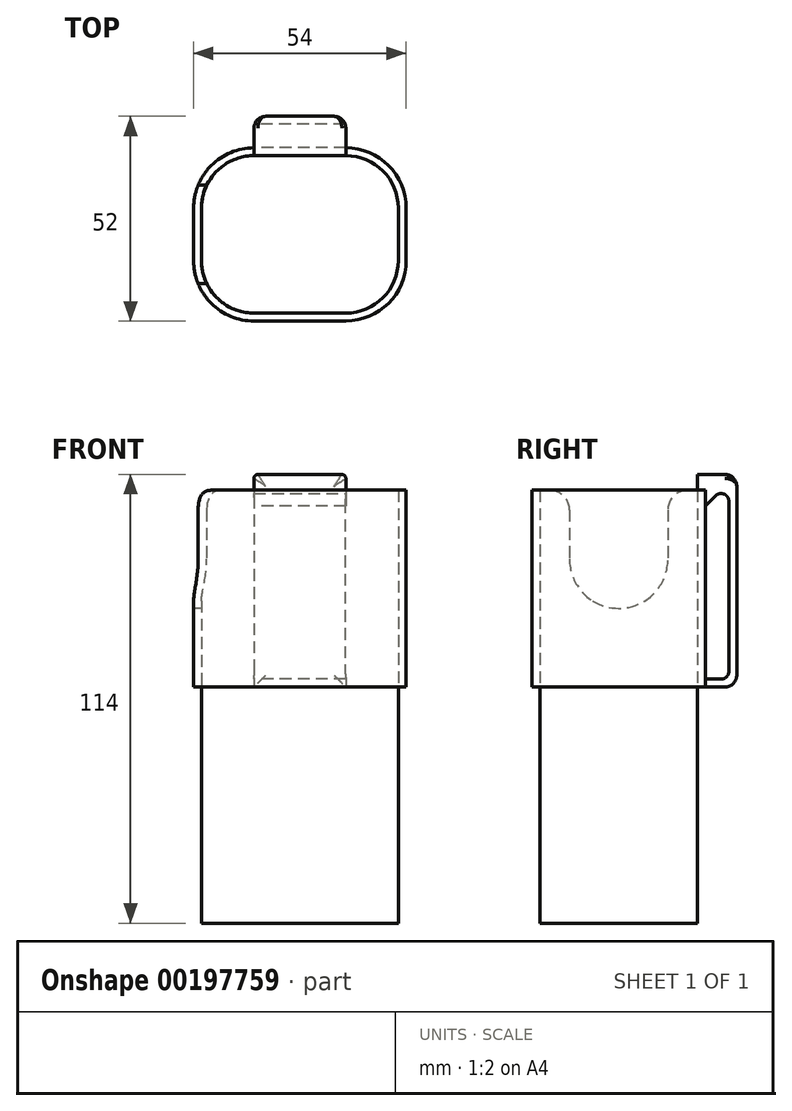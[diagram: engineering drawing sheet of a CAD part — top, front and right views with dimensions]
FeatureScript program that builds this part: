
annotation { "Feature Type Name" : "Feature", "Feature Type Description" : "" }
export const myFeature = defineFeature(function(context is Context, id is Id, definition is map)
    precondition{}
    {
        {
            assignVariable(context, id + "F0", {"name" : "WIDTH", "anyValue" : 50});
        }
        {
            assignVariable(context, id + "F1", {"name" : "DEPTH", "anyValue" : 40});
        }
        {
            var Q0;
            Q0=qCreatedBy(makeId("Top.planeOp"),FACE);
            var sketch = newSketch(context, id + "F2", { "sketchPlane" : qUnion([Q0])});
            skLineSegment(sketch, "E0.bottom", {"start": v(11.67, -40) * mm, "end": v(-11.67, -40) * mm});
            skLineSegment(sketch, "E0.top", {"start": v(11.67, 0) * mm, "end": v(-11.67, 0) * mm});
            skLineSegment(sketch, "E0.left", {"start": v(25, -26.67) * mm, "end": v(25, -13.33) * mm});
            skLineSegment(sketch, "E0.right", {"start": v(-25, -26.67) * mm, "end": v(-25, -13.33) * mm});
            skPoint(sketch, "E0.middle", {"position": v(0, -20) * mm});
            skPoint(sketch, "E1.visualSharp", {"position": v(-25, -40) * mm});
            skArc(sketch, "E1.filletArc", {"start": v(-25, -26.67) * mm, "mid": v(-21.1, -36.1) * mm, "end": v(-11.67, -40) * mm});
            skPoint(sketch, "E2.visualSharp", {"position": v(25, -40) * mm});
            skArc(sketch, "E2.filletArc", {"start": v(11.67, -40) * mm, "mid": v(21.1, -36.1) * mm, "end": v(25, -26.67) * mm});
            skPoint(sketch, "E3.visualSharp", {"position": v(-25, 0) * mm});
            skArc(sketch, "E3.filletArc", {"start": v(-11.67, 0) * mm, "mid": v(-21.1, -3.9) * mm, "end": v(-25, -13.33) * mm});
            skPoint(sketch, "E4.visualSharp", {"position": v(25, 0) * mm});
            skArc(sketch, "E4.filletArc", {"start": v(25, -13.33) * mm, "mid": v(21.1, -3.9) * mm, "end": v(11.67, 0) * mm});
            skSolve(sketch);
        }
        {
            var Q0;
            Q0=qSketchRegion(id+"F2",true);
            extrude(context, id + "F3", {"entities" : qUnion([Q0]), "endBound" : BoundingType.SYMMETRIC, "depth" : 120 * mm, "hasSecondDirection" : true, "secondDirectionOppositeDirection" : true, "secondDirectionDepth" : 25 * mm});
        }
        {
            assignVariable(context, id + "F4", {"name" : "THICKNESS", "anyValue" : 2});
        }
        {
            assignVariable(context, id + "F5", {"name" : "BELT_HOLE_THICKNESS", "anyValue" : 6});
        }
        {
            var Q0;
            Q0=qCreatedBy(makeId("Top.planeOp"),FACE);
            cPlane(context, id + "F6", {"entities" : qUnion([Q0]), "cplaneType" : CPlaneType.OFFSET, "offset" : 50 * mm, "width" : 150 * mm, "height" : 150 * mm});
        }
        {
            var Q0;
            Q0=qCreatedBy(makeId("Top.planeOp"),FACE);
            var sketch = newSketch(context, id + "F7", { "sketchPlane" : qUnion([Q0])});
            skLineSegment(sketch, "E5.0", {"start": v(27, -26.67) * mm, "end": v(27, -13.33) * mm});
            skArc(sketch, "E5.1", {"start": v(11.67, -42) * mm, "mid": v(22.5, -37.5) * mm, "end": v(27, -26.67) * mm});
            skArc(sketch, "E5.2", {"start": v(27, -13.33) * mm, "mid": v(22.5, -2.5) * mm, "end": v(11.67, 2) * mm});
            skLineSegment(sketch, "E5.3", {"start": v(-11.67, -42) * mm, "end": v(11.67, -42) * mm});
            skLineSegment(sketch, "E5.4", {"start": v(11.67, 2) * mm, "end": v(-11.67, 2) * mm});
            skArc(sketch, "E5.5", {"start": v(-11.67, 2) * mm, "mid": v(-22.5, -2.5) * mm, "end": v(-27, -13.33) * mm});
            skLineSegment(sketch, "E5.6", {"start": v(-27, -13.33) * mm, "end": v(-27, -26.67) * mm});
            skArc(sketch, "E5.7", {"start": v(-27, -26.67) * mm, "mid": v(-22.5, -37.5) * mm, "end": v(-11.67, -42) * mm});
            skSolve(sketch);
        }
        {
            var Q0;
            Q0=qSketchRegion(id+"F7",true);
            var Q1;
            Q1=qCreatedBy(id+"F6.planeOp",FACE);
            extrude(context, id + "F8", {"entities" : qUnion([Q0]), "endBound" : BoundingType.UP_TO_SURFACE, "endBoundEntityFace" : qUnion([Q1]), "offsetDistance" : 25 * mm, "depth" : 40 * mm});
        }
        {
            var Q0;
            Q0=qCreatedBy(makeId("Right.planeOp"),FACE);
            var sketch = newSketch(context, id + "F9", { "sketchPlane" : qUnion([Q0])});
            skLineSegment(sketch, "E6", {"start": v(0, 54) * mm, "end": v(10, 54) * mm});
            skLineSegment(sketch, "E7", {"start": v(10, 54) * mm, "end": v(10, 0) * mm});
            skLineSegment(sketch, "E8", {"start": v(10, 0) * mm, "end": v(0, 0) * mm});
            skLineSegment(sketch, "E9", {"start": v(0, 0) * mm, "end": v(0, 54) * mm});
            skLineSegment(sketch, "E10", {"start": v(8, 2) * mm, "end": v(8, 52) * mm});
            skLineSegment(sketch, "E11", {"start": v(8, 52) * mm, "end": v(2, 46) * mm});
            skLineSegment(sketch, "E12", {"start": v(2, 2) * mm, "end": v(8, 2) * mm});
            skLineSegment(sketch, "E13", {"start": v(2, 46) * mm, "end": v(2, 2) * mm});
            skSolve(sketch);
        }
        {
            var Q0;
            Q0=qSketchRegion(id+"F9",true);
            extrude(context, id + "F10", {"entities" : qUnion([Q0]), "operationType" : NewBodyOperationType.ADD, "endBound" : BoundingType.SYMMETRIC, "offsetDistance" : 25 * mm, "depth" : (getVariable(context, 'WIDTH') - getVariable(context, 'DEPTH') * 2 / 3) * mm});
        }
        {
            var Q0;
            Q0=qSketchRegion(id+"F2",true);
            extrude(context, id + "F11", {"entities" : qUnion([Q0]), "operationType" : NewBodyOperationType.REMOVE, "endBound" : BoundingType.THROUGH_ALL, "offsetDistance" : 25 * mm, "depth" : 25 * mm});
        }
        {
            var Q0;
            Q0=makeQuery(id+"F8.opExtrude","SWEPT_FACE",FACE,{"disambiguationData":[OSD([sQuery(id+"F7.wireOp",EDGE,"E5.6")])]});
            var sketch = newSketch(context, id + "F12", { "sketchPlane" : qUnion([Q0])});
            skArc(sketch, "E14", {"start": v(7.5, 45) * mm, "mid": v(6.04, 48.54) * mm, "end": v(2.5, 50) * mm});
            skArc(sketch, "E15", {"start": v(7.5, 32.5) * mm, "mid": v(20, 20) * mm, "end": v(32.5, 32.5) * mm});
            skArc(sketch, "E16", {"start": v(37.5, 50) * mm, "mid": v(33.96, 48.54) * mm, "end": v(32.5, 45) * mm});
            skLineSegment(sketch, "E17", {"start": v(20, 50) * mm, "end": v(20, 0) * mm, "construction": true});
            skLineSegment(sketch, "E18", {"start": v(2.5, 50) * mm, "end": v(37.5, 50) * mm});
            skLineSegment(sketch, "E19", {"start": v(7.5, 45) * mm, "end": v(7.5, 32.5) * mm});
            skLineSegment(sketch, "E20", {"start": v(32.5, 32.5) * mm, "end": v(32.5, 45) * mm});
            skSolve(sketch);
        }
        {
            var Q0;
            Q0 = qSketchRegion(id + "F12", true);
            var Q1;
            Q1=qCreatedBy(makeId("Right.planeOp"),FACE);
            extrude(context, id + "F13", {"entities" : qUnion([Q0]), "operationType" : NewBodyOperationType.REMOVE, "endBound" : BoundingType.UP_TO_SURFACE, "oppositeDirection" : true, "depth" : 25 * mm, "endBoundEntityFace" : qUnion([Q1]), "offsetDistance" : 25 * mm});
        }
        {
            var Q0;
            {var subQ0=sQuery(id+"F9.wireOp",EDGE,"E8");var subQ1=sQuery(id+"F7.wireOp",EDGE,"Tw5tcOzl-Z9Yj-e21Q-BQxL-FKIylbXYothm.left");var subQ2=sQuery(id+"F7.wireOp",EDGE,"Tw5tcOzl-Z9Yj-e21Q-BQxL-FKIylbXYothm.bottom");Q0=makeQuery(id+"F10.boolean.opBoolean","SPLIT",EDGE,{"disambiguationData":[TD([makeQuery(id+"F10.opExtrude","SWEPT_FACE",FACE,{"disambiguationData":[OSD([subQ0])]})])],"derivedFrom":makeQuery(id+"F8.opExtrude","SWEPT_EDGE",EDGE,{"disambiguationData":[OSD([subQ2,subQ1])]})});}
            var Q1;
            {var subQ0=sQuery(id+"F9.wireOp",EDGE,"GKxuiEhX-KDhd-fcK0-KWfq-KR3722g3tp84");var subQ1=sQuery(id+"F7.wireOp",EDGE,"Tw5tcOzl-Z9Yj-e21Q-BQxL-FKIylbXYothm.bottom");var subQ3=sQuery(id+"F7.wireOp",EDGE,"Tw5tcOzl-Z9Yj-e21Q-BQxL-FKIylbXYothm.left");Q1=makeQuery(id+"F10.boolean.opBoolean","SPLIT",EDGE,{"disambiguationData":[TD([makeQuery(id+"F10.opExtrude","SWEPT_FACE",FACE,{"disambiguationData":[OSD([subQ0])]})])],"derivedFrom":makeQuery(id+"F8.opExtrude","SWEPT_EDGE",EDGE,{"disambiguationData":[OSD([subQ1,subQ3])]})});}
            var Q2;
            {var subQ0=sQuery(id+"F9.wireOp",EDGE,"E8");var subQ1=sQuery(id+"F7.wireOp",EDGE,"Tw5tcOzl-Z9Yj-e21Q-BQxL-FKIylbXYothm.right");var subQ2=sQuery(id+"F7.wireOp",EDGE,"Tw5tcOzl-Z9Yj-e21Q-BQxL-FKIylbXYothm.bottom");Q2=makeQuery(id+"F10.boolean.opBoolean","SPLIT",EDGE,{"disambiguationData":[TD([makeQuery(id+"F10.opExtrude","SWEPT_FACE",FACE,{"disambiguationData":[OSD([subQ0])]})])],"derivedFrom":makeQuery(id+"F8.opExtrude","SWEPT_EDGE",EDGE,{"disambiguationData":[OSD([subQ2,subQ1])]})});}
            var Q3;
            {var subQ0=sQuery(id+"F9.wireOp",EDGE,"GKxuiEhX-KDhd-fcK0-KWfq-KR3722g3tp84");var subQ1=sQuery(id+"F7.wireOp",EDGE,"Tw5tcOzl-Z9Yj-e21Q-BQxL-FKIylbXYothm.bottom");var subQ3=sQuery(id+"F7.wireOp",EDGE,"Tw5tcOzl-Z9Yj-e21Q-BQxL-FKIylbXYothm.right");Q3=makeQuery(id+"F10.boolean.opBoolean","SPLIT",EDGE,{"disambiguationData":[TD([makeQuery(id+"F10.opExtrude","SWEPT_FACE",FACE,{"disambiguationData":[OSD([subQ0])]})])],"derivedFrom":makeQuery(id+"F8.opExtrude","SWEPT_EDGE",EDGE,{"disambiguationData":[OSD([subQ1,subQ3])]})});}
            var Q4;
            Q4=makeQuery(id+"F11.boolean.opBoolean","INTERSECT",EDGE,{"derivedFrom":[makeQuery(id+"F10.boolean.opBoolean","MERGE",FACE,{"derivedFrom":[makeQuery(id+"F8.opExtrude","CAP_FACE",FACE,{"disambiguationData":[OSD([dummyQuery(id+"F6.planeOp",FACE)])],"isStart":false}),makeQuery(id+"F10.opExtrude","SWEPT_FACE",FACE,{"disambiguationData":[OSD([sQuery(id+"F9.wireOp",EDGE,"E6")])]})]}),makeQuery(id+"F11.opExtrude","SWEPT_FACE",FACE,{"disambiguationData":[OSD([sQuery(id+"F2.wireOp",EDGE,"E0.top")])]})]});
            var Q5;
            Q5=makeQuery(id+"F10.opExtrude","CAP_EDGE",EDGE,{"disambiguationData":[OSD([sQuery(id+"F9.wireOp",EDGE,"E7")])],"isStart":false});
            var Q6;
            Q6=makeQuery(id+"F10.opExtrude","CAP_EDGE",EDGE,{"disambiguationData":[OSD([sQuery(id+"F9.wireOp",EDGE,"E7")])],"isStart":true});
            var Q7;
            Q7=makeQuery(id+"F10.opExtrude","SWEPT_EDGE",EDGE,{"disambiguationData":[OSD([sQuery(id+"F9.wireOp",EDGE,"E7"),sQuery(id+"F9.wireOp",EDGE,"E8")])]});
            var Q8;
            Q8=makeQuery(id+"F10.opExtrude","SWEPT_EDGE",EDGE,{"disambiguationData":[OSD([sQuery(id+"F9.wireOp",EDGE,"E6"),sQuery(id+"F9.wireOp",EDGE,"E7")])]});
            var Q9;
            Q9=makeQuery(id+"F10.opExtrude","SWEPT_EDGE",EDGE,{"disambiguationData":[OSD([sQuery(id+"F9.wireOp",EDGE,"E6"),sQuery(id+"F9.wireOp",EDGE,"E9")])]});
            fillet(context, id + "F14", {"entities" : qUnion([Q0, Q1, Q2, Q3, Q4, Q5, Q6, Q7, Q8, Q9]), "radius" : (getVariable(context, 'BELT_HOLE_THICKNESS') / 2) * mm, "tangentPropagation" : true, "allowEdgeOverflow" : false});
        }
        {
            var Q0;
            Q0=makeQuery(id+"F10.opExtrude","SWEPT_EDGE",EDGE,{"disambiguationData":[OSD([sQuery(id+"F9.wireOp",EDGE,"E10"),sQuery(id+"F9.wireOp",EDGE,"E11")])]});
            var Q1;
            Q1=makeQuery(id+"F10.opExtrude","SWEPT_EDGE",EDGE,{"disambiguationData":[OSD([sQuery(id+"F9.wireOp",EDGE,"E11"),sQuery(id+"F9.wireOp",EDGE,"E13")])]});
            var Q2;
            Q2=makeQuery(id+"F10.opExtrude","SWEPT_EDGE",EDGE,{"disambiguationData":[OSD([sQuery(id+"F9.wireOp",EDGE,"E12"),sQuery(id+"F9.wireOp",EDGE,"E13")])]});
            var Q3;
            Q3=makeQuery(id+"F10.opExtrude","SWEPT_EDGE",EDGE,{"disambiguationData":[OSD([sQuery(id+"F9.wireOp",EDGE,"E10"),sQuery(id+"F9.wireOp",EDGE,"E12")])]});
            var Q4;
            Q4=makeQuery(id+"F10.boolean.opBoolean","INTERSECT",EDGE,{"derivedFrom":[makeQuery(id+"F8.opExtrude","CAP_FACE",FACE,{"disambiguationData":[OSD([dummyQuery(id+"F6.planeOp",FACE)])],"isStart":false}),makeQuery(id+"F10.opExtrude","CAP_FACE",FACE,{"disambiguationData":[OSD([sQuery(id+"F9.wireOp",EDGE,"E6"),sQuery(id+"F9.wireOp",EDGE,"E7"),sQuery(id+"F9.wireOp",EDGE,"E8"),sQuery(id+"F9.wireOp",EDGE,"E9"),sQuery(id+"F9.wireOp",EDGE,"E10"),sQuery(id+"F9.wireOp",EDGE,"E11"),sQuery(id+"F9.wireOp",EDGE,"E12"),sQuery(id+"F9.wireOp",EDGE,"E13"),sQuery(id+"F9.wireOp",EDGE,"EpreTBwx-W1Xm-lshD-LFvw-tCIKyT3mJ0il")])],"isStart":false})]});
            var Q5;
            Q5=makeQuery(id+"F10.boolean.opBoolean","INTERSECT",EDGE,{"derivedFrom":[makeQuery(id+"F8.opExtrude","CAP_FACE",FACE,{"disambiguationData":[OSD([dummyQuery(id+"F6.planeOp",FACE)])],"isStart":false}),makeQuery(id+"F10.opExtrude","CAP_FACE",FACE,{"disambiguationData":[OSD([sQuery(id+"F9.wireOp",EDGE,"E6"),sQuery(id+"F9.wireOp",EDGE,"E7"),sQuery(id+"F9.wireOp",EDGE,"E8"),sQuery(id+"F9.wireOp",EDGE,"E9"),sQuery(id+"F9.wireOp",EDGE,"E10"),sQuery(id+"F9.wireOp",EDGE,"E11"),sQuery(id+"F9.wireOp",EDGE,"E12"),sQuery(id+"F9.wireOp",EDGE,"E13"),sQuery(id+"F9.wireOp",EDGE,"EpreTBwx-W1Xm-lshD-LFvw-tCIKyT3mJ0il")])],"isStart":true})]});
            fillet(context, id + "F15", {"entities" : qUnion([Q0, Q1, Q2, Q3, Q4, Q5]), "radius" : (getVariable(context, 'THICKNESS')) * mm, "tangentPropagation" : true, "allowEdgeOverflow" : false});
        }
        {
            var Q0;
            Q0=makeQuery(id+"F11.boolean.opBoolean","INTERSECT",EDGE,{"derivedFrom":[makeQuery(id+"F8.opExtrude","CAP_FACE",FACE,{"disambiguationData":[OSD([dummyQuery(id+"F6.planeOp",FACE)])],"isStart":false}),makeQuery(id+"F11.opExtrude","SWEPT_FACE",FACE,{"disambiguationData":[OSD([sQuery(id+"F2.wireOp",EDGE,"E0.bottom")])]})]});
            var Q1;
            Q1=makeQuery(id+"F8.opExtrude","CAP_EDGE",EDGE,{"disambiguationData":[OSD([sQuery(id+"F7.wireOp",EDGE,"b42710f8-3539-4a70-8dba-9079cd12ec19.2")])],"isStart":true});
            var Q2;
            {var subQ2=sQuery(id+"F9.wireOp",EDGE,"E8");var subQ3=sQuery(id+"F7.wireOp",EDGE,"b42710f8-3539-4a70-8dba-9079cd12ec19.7");var subQ4=sQuery(id+"F7.wireOp",EDGE,"b42710f8-3539-4a70-8dba-9079cd12ec19.6");Q2=makeQuery(id+"F10.boolean.opBoolean","SPLIT",EDGE,{"disambiguationData":[TD([makeQuery(id+"F10.opExtrude","SWEPT_FACE",FACE,{"disambiguationData":[OSD([subQ2])]})])],"derivedFrom":makeQuery(id+"F8.opExtrude","SWEPT_EDGE",EDGE,{"disambiguationData":[OSD([subQ4,subQ3])]})});}
            var Q3;
            {var subQ0=sQuery(id+"F7.wireOp",EDGE,"b42710f8-3539-4a70-8dba-9079cd12ec19.7");var subQ3=sQuery(id+"F9.wireOp",EDGE,"E8");var subQ4=sQuery(id+"F7.wireOp",EDGE,"b42710f8-3539-4a70-8dba-9079cd12ec19.3");Q3=makeQuery(id+"F10.boolean.opBoolean","SPLIT",EDGE,{"disambiguationData":[TD([makeQuery(id+"F10.opExtrude","SWEPT_FACE",FACE,{"disambiguationData":[OSD([subQ3])]})])],"derivedFrom":makeQuery(id+"F8.opExtrude","SWEPT_EDGE",EDGE,{"disambiguationData":[OSD([subQ4,subQ0])]})});}
            var Q4;
            Q4=makeQuery(id+"F10.opExtrude","CAP_EDGE",EDGE,{"disambiguationData":[OSD([sQuery(id+"F9.wireOp",EDGE,"E6")])],"isStart":true});
            var Q5;
            Q5=makeQuery(id+"F10.opExtrude","CAP_EDGE",EDGE,{"disambiguationData":[OSD([sQuery(id+"F9.wireOp",EDGE,"E6")])],"isStart":false});
            fillet(context, id + "F16", {"entities" : qUnion([Q0, Q1, Q2, Q3, Q4, Q5]), "radius" : (getVariable(context, 'THICKNESS') / 2) * mm, "tangentPropagation" : true, "allowEdgeOverflow" : false});
        }
    });
